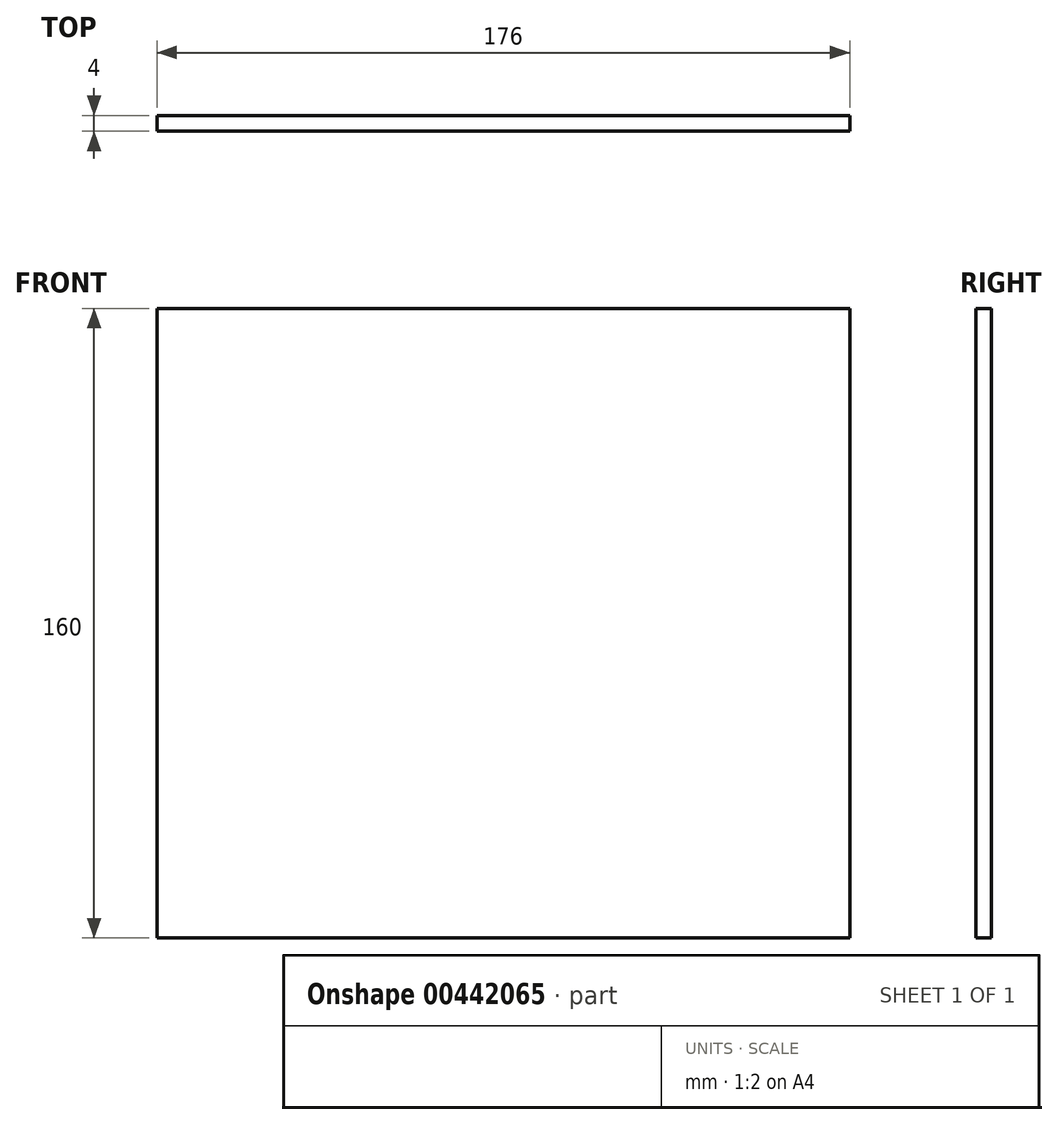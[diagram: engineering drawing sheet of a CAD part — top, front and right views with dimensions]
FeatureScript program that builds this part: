
annotation { "Feature Type Name" : "Feature", "Feature Type Description" : "" }
export const myFeature = defineFeature(function(context is Context, id is Id, definition is map)
    precondition{}
    {
        {
            var Q0;
            Q0=qCreatedBy(makeId("Front.planeOp"),FACE);
            var sketch = newSketch(context, id + "F0", { "sketchPlane" : qUnion([Q0])});
            skLineSegment(sketch, "E0.bottom", {"start": v(88, -80) * mm, "end": v(-88, -80) * mm});
            skLineSegment(sketch, "E0.top", {"start": v(88, 80) * mm, "end": v(-88, 80) * mm});
            skLineSegment(sketch, "E0.left", {"start": v(88, -80) * mm, "end": v(88, 80) * mm});
            skLineSegment(sketch, "E0.right", {"start": v(-88, -80) * mm, "end": v(-88, 80) * mm});
            skPoint(sketch, "E0.middle", {"position": v(0, 0) * mm});
            skSolve(sketch);
        }
        {
            var Q0;
            Q0=makeQuery(id+"F0.imprint","IMPRINT",FACE,{"disambiguationData":[TD([[makeQuery(id+"F0.imprint","IMPRINT",EDGE,{"derivedFrom":sQuery(id+"F0.wireOp",EDGE,"E0.bottom")}),-1.0]])]});
            extrude(context, id + "F1", {"entities" : qUnion([Q0]), "depth" : 4 * mm});
        }
    });
